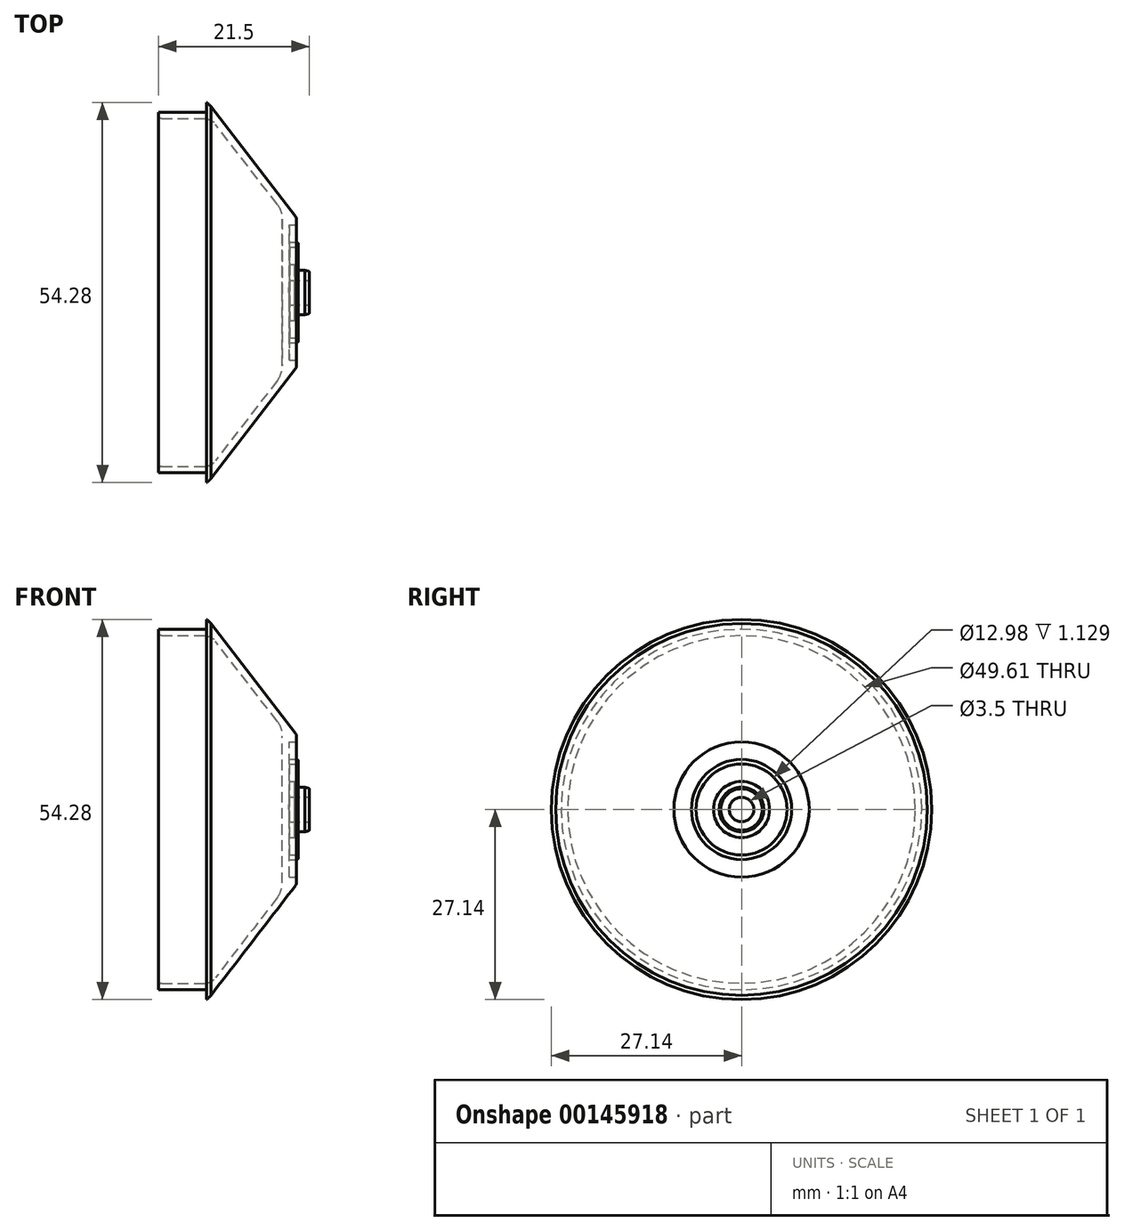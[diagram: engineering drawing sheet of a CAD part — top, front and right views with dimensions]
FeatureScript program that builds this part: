
annotation { "Feature Type Name" : "Feature", "Feature Type Description" : "" }
export const myFeature = defineFeature(function(context is Context, id is Id, definition is map)
    precondition{}
    {
        {
            var Q0;
            Q0=qCreatedBy(makeId("Front.planeOp"),FACE);
            var sketch = newSketch(context, id + "F0", { "sketchPlane" : qUnion([Q0])});
            skArc(sketch, "E0", {"start": v(2.42, 9.65) * mm, "mid": v(2.6, 9.73) * mm, "end": v(2.67, 9.9) * mm});
            skArc(sketch, "E1", {"start": v(2.93, 6.9) * mm, "mid": v(2.85, 7.08) * mm, "end": v(2.67, 7.15) * mm});
            skArc(sketch, "E2", {"start": v(2.8, 6.5) * mm, "mid": v(2.9, 6.53) * mm, "end": v(2.93, 6.62) * mm});
            skLineSegment(sketch, "E3", {"start": v(1.67, 4) * mm, "end": v(1.67, 6.5) * mm});
            skLineSegment(sketch, "E4", {"start": v(4.49, 1.75) * mm, "end": v(4.49, 2.97) * mm});
            skLineSegment(sketch, "E5", {"start": v(2.37, 3.19) * mm, "end": v(2.37, 4) * mm});
            skLineSegment(sketch, "E6", {"start": v(4.37, 3.05) * mm, "end": v(3.88, 3.18) * mm});
            skLineSegment(sketch, "E7", {"start": v(2.37, 3.19) * mm, "end": v(3.84, 3.19) * mm});
            skLineSegment(sketch, "E8", {"start": v(1.67, 7.15) * mm, "end": v(2.67, 7.15) * mm});
            skArc(sketch, "E9", {"start": v(3.88, 3.18) * mm, "mid": v(3.86, 3.18) * mm, "end": v(3.84, 3.19) * mm});
            skLineSegment(sketch, "E10", {"start": v(4.49, 1.75) * mm, "end": v(1.65, 1.75) * mm});
            skLineSegment(sketch, "E11", {"start": v(1.65, 1.75) * mm, "end": v(1.58, 0) * mm});
            skArc(sketch, "E12", {"start": v(4.49, 2.97) * mm, "mid": v(4.44, 3.02) * mm, "end": v(4.37, 3.05) * mm});
            skLineSegment(sketch, "E13", {"start": v(1.58, 0) * mm, "end": v(0.8, 0) * mm});
            skLineSegment(sketch, "E14", {"start": v(-20.28, 0) * mm, "end": v(-20.28, 27.66) * mm});
            skLineSegment(sketch, "E15", {"start": v(-17.01, 25.73) * mm, "end": v(-10.18, 25.73) * mm});
            skLineSegment(sketch, "E16", {"start": v(1.67, 9.65) * mm, "end": v(1.67, 7.15) * mm});
            skLineSegment(sketch, "E17", {"start": v(1.67, 9.65) * mm, "end": v(2.42, 9.65) * mm});
            skLineSegment(sketch, "E18", {"start": v(2.93, 6.9) * mm, "end": v(2.93, 6.62) * mm});
            skLineSegment(sketch, "E19", {"start": v(2.8, 6.5) * mm, "end": v(1.67, 6.5) * mm});
            skLineSegment(sketch, "E20", {"start": v(1.67, 4) * mm, "end": v(2.37, 4) * mm});
            skPoint(sketch, "E21.visualSharp", {"position": v(-17.01, 25.44) * mm});
            skLineSegment(sketch, "E22", {"start": v(-11.26, 27.54) * mm, "end": v(-15.92, 28.2) * mm});
            skLineSegment(sketch, "E23", {"start": v(-17.01, 27.25) * mm, "end": v(-17.01, 25.73) * mm});
            skPoint(sketch, "E24.visualSharp", {"position": v(-17.01, 28.35) * mm});
            skArc(sketch, "E24.filletArc", {"start": v(-15.92, 28.2) * mm, "mid": v(-16.68, 27.97) * mm, "end": v(-17.01, 27.25) * mm});
            skPoint(sketch, "E25.visualSharp", {"position": v(-10.18, 27.4) * mm});
            skArc(sketch, "E25.filletArc", {"start": v(-9.54, 26.52) * mm, "mid": v(-10.3, 27.2) * mm, "end": v(-11.26, 27.54) * mm});
            skLineSegment(sketch, "E26", {"start": v(-10.18, 25.73) * mm, "end": v(-10.18, 27.14) * mm});
            skLineSegment(sketch, "E27", {"start": v(-10.5, 24.8) * mm, "end": v(-16.57, 24.8) * mm});
            skLineSegment(sketch, "E28", {"start": v(-17.01, 25.73) * mm, "end": v(-17.01, 25.25) * mm});
            skPoint(sketch, "E29.visualSharp", {"position": v(-17.01, 24.8) * mm});
            skArc(sketch, "E29.filletArc", {"start": v(-17.01, 25.25) * mm, "mid": v(-16.88, 24.93) * mm, "end": v(-16.57, 24.8) * mm});
            skLineSegment(sketch, "E30", {"start": v(2.67, 9.9) * mm, "end": v(2.67, 10.43) * mm});
            skLineSegment(sketch, "E31", {"start": v(2.53, 10.85) * mm, "end": v(-9.54, 26.52) * mm});
            skPoint(sketch, "E32.visualSharp", {"position": v(2.67, 10.67) * mm});
            skArc(sketch, "E32.filletArc", {"start": v(2.67, 10.43) * mm, "mid": v(2.64, 10.65) * mm, "end": v(2.53, 10.85) * mm});
            skLineSegment(sketch, "E33", {"start": v(-8.91, 24.03) * mm, "end": v(-0.08, 12.57) * mm});
            skLineSegment(sketch, "E34", {"start": v(0.63, 10.5) * mm, "end": v(0.63, 0) * mm});
            skPoint(sketch, "E34.endSnap0", {"position": v(1.18, 0) * mm});
            skLineSegment(sketch, "E35", {"start": v(0.63, 0) * mm, "end": v(0.8, 0) * mm});
            skPoint(sketch, "E36.visualSharp", {"position": v(0.63, 11.65) * mm});
            skArc(sketch, "E36.filletArc", {"start": v(0.63, 10.5) * mm, "mid": v(0.45, 11.6) * mm, "end": v(-0.08, 12.57) * mm});
            skPoint(sketch, "E37.visualSharp", {"position": v(-9.51, 24.8) * mm});
            skArc(sketch, "E37.filletArc", {"start": v(-8.91, 24.03) * mm, "mid": v(-9.61, 24.6) * mm, "end": v(-10.5, 24.8) * mm});
            skSolve(sketch);
        }
        {
            var Q0;
            Q0=makeQuery(id+"F0.imprint","IMPRINT",FACE,{"disambiguationData":[TD([[makeQuery(id+"F0.imprint","IMPRINT",EDGE,{"derivedFrom":sQuery(id+"F0.wireOp",EDGE,"E0")}),1.0]])]});
            var Q1;
            Q1=sQuery(id+"F0.wireOp",EDGE,"E13");
            revolve(context, id + "F1", {"entities" : qUnion([Q0]), "axis" : qUnion([Q1]), "revolveType" : RevolveType.FULL});
        }
    });
